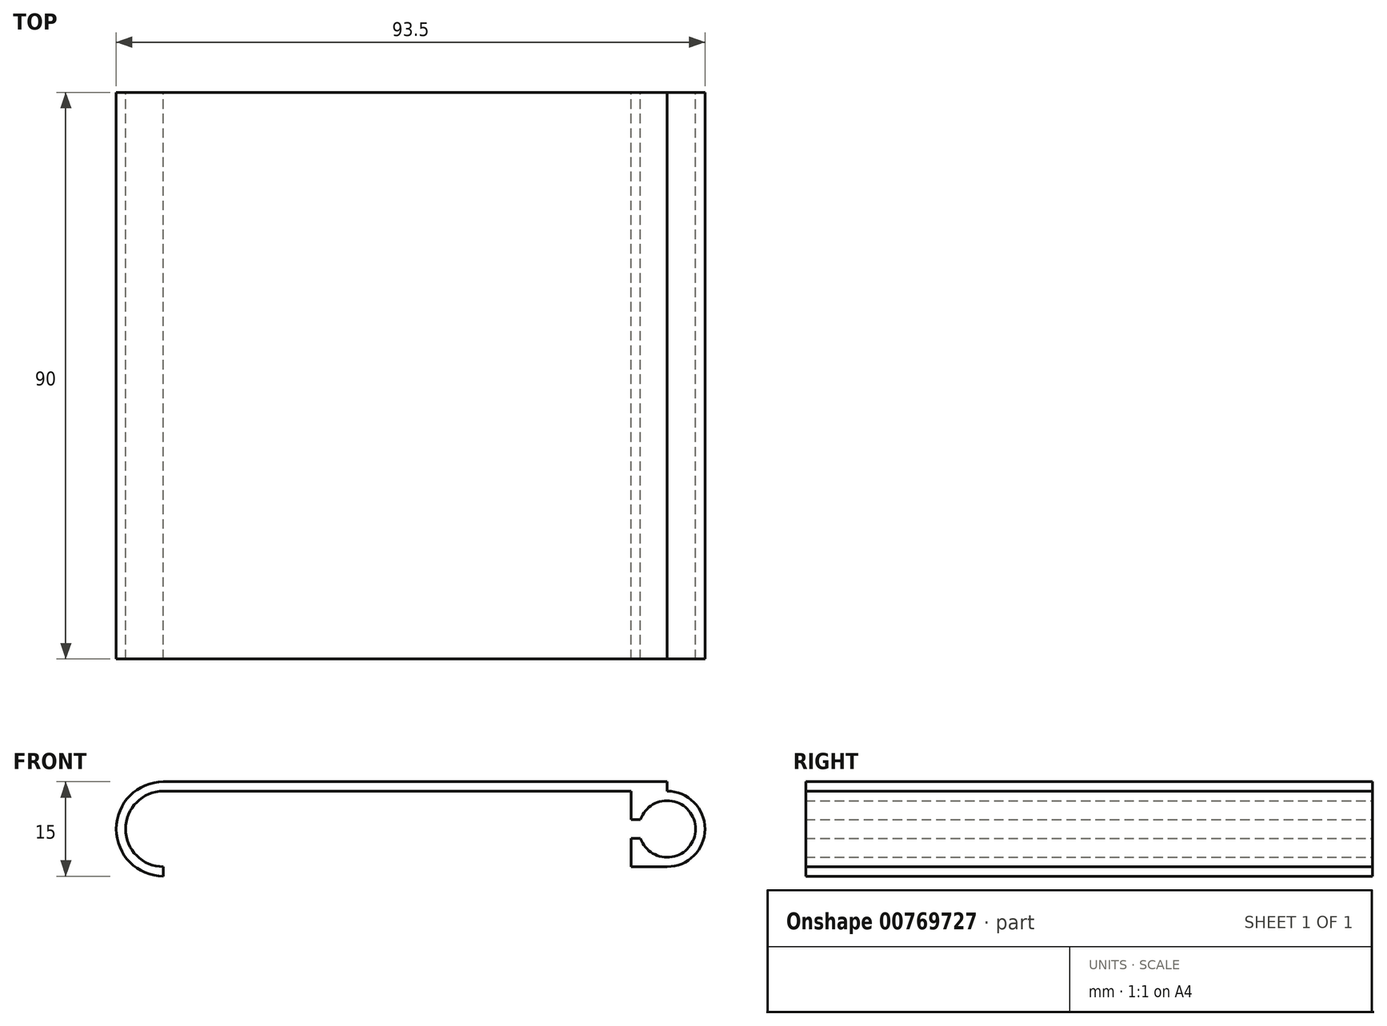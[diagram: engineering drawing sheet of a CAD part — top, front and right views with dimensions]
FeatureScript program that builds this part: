
annotation { "Feature Type Name" : "Feature", "Feature Type Description" : "" }
export const myFeature = defineFeature(function(context is Context, id is Id, definition is map)
    precondition{}
    {
        {
            var Q0;
            Q0=qCreatedBy(makeId("Front.planeOp"),FACE);
            var sketch = newSketch(context, id + "F0", { "sketchPlane" : qUnion([Q0])});
            skLineSegment(sketch, "E0.bottom", {"start": v(40, 7.5) * mm, "end": v(-40, 7.5) * mm});
            skLineSegment(sketch, "E0.top", {"start": v(40, -7.5) * mm, "end": v(-40, -7.5) * mm});
            skPoint(sketch, "E0.middle", {"position": v(0, 0) * mm});
            skArc(sketch, "E1", {"start": v(-40, 7.5) * mm, "mid": v(-47.5, 0) * mm, "end": v(-40, -7.5) * mm});
            skArc(sketch, "E2", {"start": v(40, 7.5) * mm, "mid": v(47.5, 0) * mm, "end": v(40, -7.5) * mm});
            skSolve(sketch);
        }
        {
            var Q0;
            Q0=qSketchRegion(id+"F0",true);
            extrude(context, id + "F1", {"entities" : qUnion([Q0]), "depth" : 90 * mm, "offsetDistance" : 25 * mm});
        }
        {
            var Q0;
            Q0=makeQuery(id+"F1.opExtrude","CAP_FACE",FACE,{"disambiguationData":[OSD([sQuery(id+"F0.wireOp",EDGE,"E0.bottom"),sQuery(id+"F0.wireOp",EDGE,"E0.top"),sQuery(id+"F0.wireOp",EDGE,"E1"),sQuery(id+"F0.wireOp",EDGE,"E2")])],"isStart":false});
            var Q1;
            Q1=makeQuery(id+"F1.opExtrude","CAP_FACE",FACE,{"disambiguationData":[OSD([sQuery(id+"F0.wireOp",EDGE,"E0.bottom"),sQuery(id+"F0.wireOp",EDGE,"E0.top"),sQuery(id+"F0.wireOp",EDGE,"E1"),sQuery(id+"F0.wireOp",EDGE,"E2")])],"isStart":true});
            shell(context, id + "F2", {"entities" : qUnion([Q0, Q1]), "thickness" : 1.5 * mm});
        }
        {
            var Q0;
            Q0=qCreatedBy(makeId("Front.planeOp"),FACE);
            var sketch = newSketch(context, id + "F3", { "sketchPlane" : qUnion([Q0])});
            skLineSegment(sketch, "E3.0", {"start": v(40, -6) * mm, "end": v(-40, -6) * mm});
            skLineSegment(sketch, "E4.0", {"start": v(40, -7.5) * mm, "end": v(-40, -7.5) * mm});
            skArc(sketch, "E5.0", {"start": v(40, 6) * mm, "mid": v(46, 0) * mm, "end": v(40, -6) * mm});
            skArc(sketch, "E6.0", {"start": v(40, 7.5) * mm, "mid": v(47.5, 0) * mm, "end": v(40, -7.5) * mm});
            skLineSegment(sketch, "E7", {"start": v(-40, -6) * mm, "end": v(-40, -7.5) * mm});
            skLineSegment(sketch, "E8", {"start": v(40, 7.5) * mm, "end": v(40, 6) * mm});
            skSolve(sketch);
        }
        {
            var Q0;
            Q0=qSketchRegion(id+"F3",true);
            extrude(context, id + "F4", {"entities" : qUnion([Q0]), "operationType" : NewBodyOperationType.REMOVE, "endBound" : BoundingType.THROUGH_ALL, "depth" : 25 * mm, "offsetDistance" : 25 * mm});
        }
        {
            var Q0;
            Q0=qCreatedBy(makeId("Front.planeOp"),FACE);
            var sketch = newSketch(context, id + "F5", { "sketchPlane" : qUnion([Q0])});
            skArc(sketch, "E9", {"start": v(40, -6) * mm, "mid": v(46, 0) * mm, "end": v(40, 6) * mm});
            skLineSegment(sketch, "E10.0", {"start": v(40, 6) * mm, "end": v(34.26, 6) * mm});
            skLineSegment(sketch, "E11.MirrorCS", {"start": v(40, -6) * mm, "end": v(34.26, -6) * mm});
            skLineSegment(sketch, "E12", {"start": v(35.76, -1.5) * mm, "end": v(34.26, -1.5) * mm});
            skLineSegment(sketch, "E13.trimOffspring", {"start": v(34.26, -1.5) * mm, "end": v(34.26, -6) * mm});
            skArc(sketch, "E14", {"start": v(35.76, -1.5) * mm, "mid": v(44.5, 0) * mm, "end": v(35.76, 1.5) * mm});
            skLineSegment(sketch, "E15.MirrorCS", {"start": v(35.76, 1.5) * mm, "end": v(34.26, 1.5) * mm});
            skLineSegment(sketch, "E16.MirrorCS", {"start": v(34.26, 1.5) * mm, "end": v(34.26, 6) * mm});
            skSolve(sketch);
        }
        {
            var Q0;
            Q0=qSketchRegion(id+"F5",true);
            var Q1;
            Q1=makeQuery(id+"F1.opExtrude","CAP_FACE",FACE,{"disambiguationData":[OSD([sQuery(id+"F0.wireOp",EDGE,"E0.bottom"),sQuery(id+"F0.wireOp",EDGE,"E0.top"),sQuery(id+"F0.wireOp",EDGE,"E1"),sQuery(id+"F0.wireOp",EDGE,"E2")])],"isStart":false});
            extrude(context, id + "F6", {"entities" : qUnion([Q0]), "operationType" : NewBodyOperationType.ADD, "endBound" : BoundingType.UP_TO_SURFACE, "depth" : 25 * mm, "endBoundEntityFace" : qUnion([Q1]), "offsetDistance" : 25 * mm});
        }
    });
